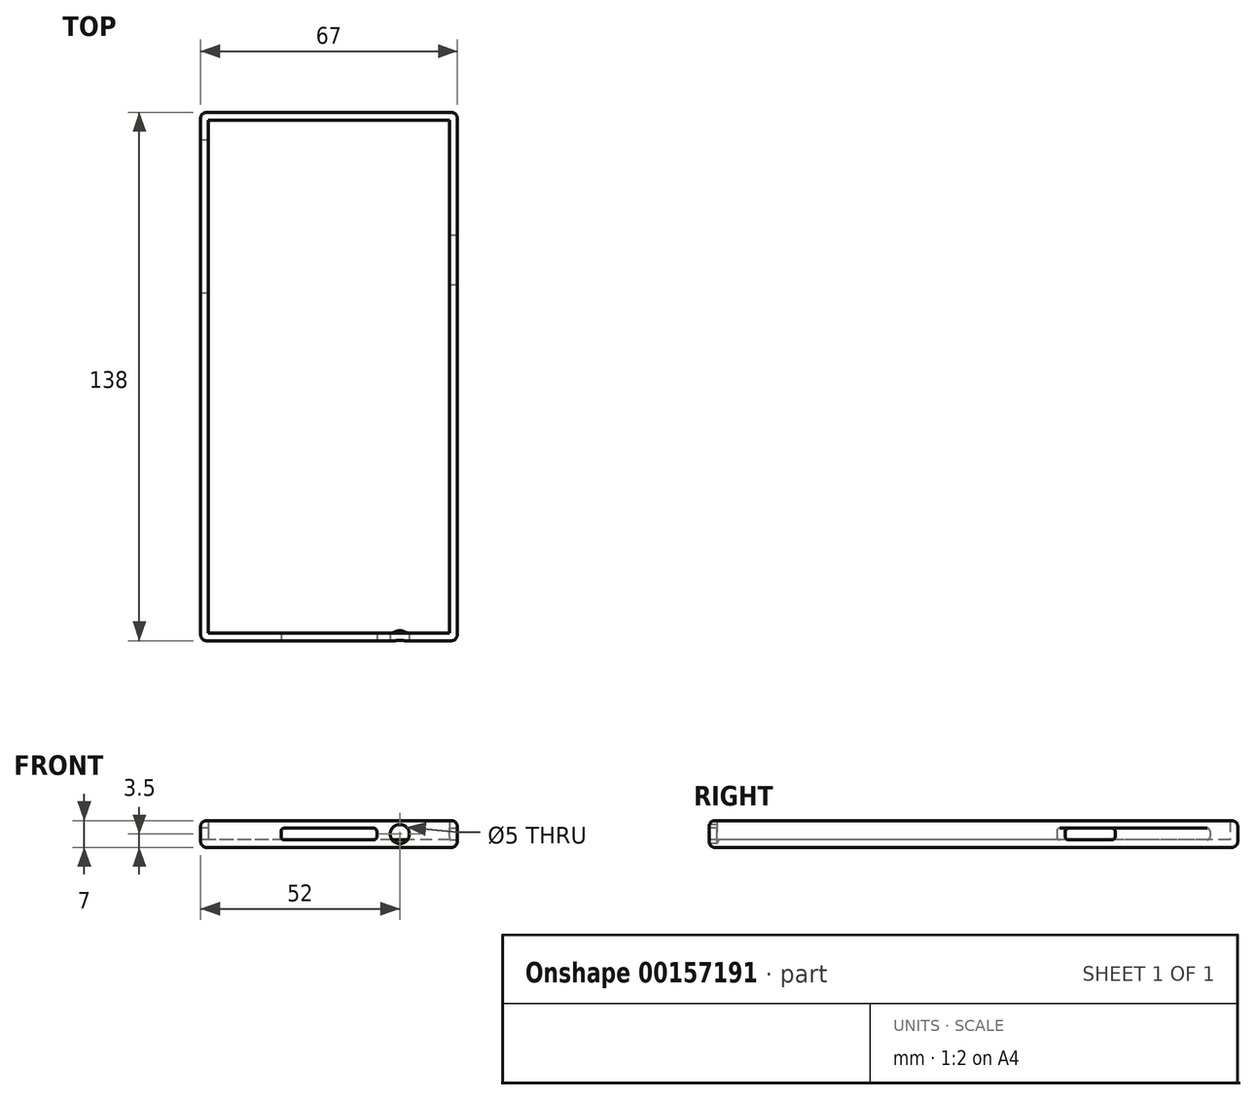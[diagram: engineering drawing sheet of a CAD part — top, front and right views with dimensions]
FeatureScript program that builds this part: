
annotation { "Feature Type Name" : "Feature", "Feature Type Description" : "" }
export const myFeature = defineFeature(function(context is Context, id is Id, definition is map)
    precondition{}
    {
        {
            var Q0;
            Q0=qCreatedBy(makeId("Top.planeOp"),FACE);
            var sketch = newSketch(context, id + "F0", { "sketchPlane" : qUnion([Q0])});
            skLineSegment(sketch, "E0.bottom", {"start": v(33.5, 69) * mm, "end": v(-33.5, 69) * mm});
            skLineSegment(sketch, "E0.top", {"start": v(33.5, -69) * mm, "end": v(-33.5, -69) * mm});
            skLineSegment(sketch, "E0.left", {"start": v(33.5, 69) * mm, "end": v(33.5, -69) * mm});
            skLineSegment(sketch, "E0.right", {"start": v(-33.5, 69) * mm, "end": v(-33.5, -69) * mm});
            skPoint(sketch, "E0.middle", {"position": v(0, 0) * mm});
            skSolve(sketch);
        }
        {
            var Q0;
            Q0 = qSketchRegion(id + "F0", true);
            extrude(context, id + "F1", {"entities" : qUnion([Q0]), "depth" : 7 * mm});
        }
        {
            var Q0;
            Q0=makeQuery(id+"F1.opExtrude","CAP_FACE",FACE,{"disambiguationData":[OSD([sQuery(id+"F0.wireOp",EDGE,"E0.bottom"),sQuery(id+"F0.wireOp",EDGE,"E0.top"),sQuery(id+"F0.wireOp",EDGE,"E0.left"),sQuery(id+"F0.wireOp",EDGE,"E0.right")])],"isStart":false});
            shell(context, id + "F2", {"entities" : qUnion([Q0]), "thickness" : 2 * mm});
        }
        {
            var Q0;
            Q0=makeQuery(id+"F1.opExtrude","SWEPT_FACE",FACE,{"disambiguationData":[OSD([sQuery(id+"F0.wireOp",EDGE,"E0.right")])]});
            var sketch = newSketch(context, id + "F3", { "sketchPlane" : qUnion([Q0])});
            skLineSegment(sketch, "E1.bottom", {"start": v(-61.02, 5) * mm, "end": v(-22.54, 5) * mm});
            skLineSegment(sketch, "E1.top", {"start": v(-61.02, 2) * mm, "end": v(-22.54, 2) * mm});
            skLineSegment(sketch, "E1.left", {"start": v(-61.78, 4.24) * mm, "end": v(-61.78, 2.76) * mm});
            skLineSegment(sketch, "E1.right", {"start": v(-21.78, 4.24) * mm, "end": v(-21.78, 2.76) * mm});
            skPoint(sketch, "E2.visualSharp", {"position": v(-61.78, 5) * mm});
            skArc(sketch, "E2.filletArc", {"start": v(-61.02, 5) * mm, "mid": v(-61.56, 4.78) * mm, "end": v(-61.78, 4.24) * mm});
            skPoint(sketch, "E3.visualSharp", {"position": v(-61.78, 2) * mm});
            skArc(sketch, "E3.filletArc", {"start": v(-61.78, 2.76) * mm, "mid": v(-61.56, 2.22) * mm, "end": v(-61.02, 2) * mm});
            skPoint(sketch, "E4.visualSharp", {"position": v(-21.78, 5) * mm});
            skArc(sketch, "E4.filletArc", {"start": v(-21.78, 4.24) * mm, "mid": v(-22, 4.78) * mm, "end": v(-22.54, 5) * mm});
            skPoint(sketch, "E5.visualSharp", {"position": v(-21.78, 2) * mm});
            skArc(sketch, "E5.filletArc", {"start": v(-22.54, 2) * mm, "mid": v(-22, 2.22) * mm, "end": v(-21.78, 2.76) * mm});
            skSolve(sketch);
        }
        {
            var Q0;
            Q0=makeQuery(id+"F3.imprint","IMPRINT",FACE,{"disambiguationData":[TD([[makeQuery(id+"F3.imprint","IMPRINT",EDGE,{"derivedFrom":sQuery(id+"F3.wireOp",EDGE,"E1.bottom")}),-1.0]])]});
            var Q1;
            Q1=makeQuery(id+"F2.opShell","OFFSET_FACE",FACE,{"disambiguationData":[OSD([sQuery(id+"F0.wireOp",EDGE,"E0.right")])]});
            extrude(context, id + "F4", {"entities" : qUnion([Q0]), "operationType" : NewBodyOperationType.REMOVE, "endBound" : BoundingType.UP_TO_SURFACE, "oppositeDirection" : true, "endBoundEntityFace" : qUnion([Q1]), "depth" : 25 * mm});
        }
        {
            var Q0;
            Q0=makeQuery(id+"F1.opExtrude","SWEPT_FACE",FACE,{"disambiguationData":[OSD([sQuery(id+"F0.wireOp",EDGE,"E0.left")])]});
            var sketch = newSketch(context, id + "F5", { "sketchPlane" : qUnion([Q0])});
            skLineSegment(sketch, "E6.bottom", {"start": v(24.76, 5) * mm, "end": v(36.24, 5) * mm});
            skLineSegment(sketch, "E6.top", {"start": v(24.76, 2) * mm, "end": v(36.24, 2) * mm});
            skLineSegment(sketch, "E6.left", {"start": v(24, 4.24) * mm, "end": v(24, 2.76) * mm});
            skLineSegment(sketch, "E6.right", {"start": v(37, 4.24) * mm, "end": v(37, 2.76) * mm});
            skPoint(sketch, "E7.visualSharp", {"position": v(24, 5) * mm});
            skArc(sketch, "E7.filletArc", {"start": v(24.76, 5) * mm, "mid": v(24.22, 4.78) * mm, "end": v(24, 4.24) * mm});
            skPoint(sketch, "E8.visualSharp", {"position": v(24, 2) * mm});
            skArc(sketch, "E8.filletArc", {"start": v(24, 2.76) * mm, "mid": v(24.22, 2.22) * mm, "end": v(24.76, 2) * mm});
            skPoint(sketch, "E9.visualSharp", {"position": v(37, 5) * mm});
            skArc(sketch, "E9.filletArc", {"start": v(37, 4.24) * mm, "mid": v(36.78, 4.78) * mm, "end": v(36.24, 5) * mm});
            skPoint(sketch, "E10.visualSharp", {"position": v(37, 2) * mm});
            skArc(sketch, "E10.filletArc", {"start": v(36.24, 2) * mm, "mid": v(36.78, 2.22) * mm, "end": v(37, 2.76) * mm});
            skSolve(sketch);
        }
        {
            var Q0;
            Q0 = qSketchRegion(id + "F5", true);
            var Q1;
            Q1=makeQuery(id+"F2.opShell","OFFSET_FACE",FACE,{"disambiguationData":[OSD([sQuery(id+"F0.wireOp",EDGE,"E0.left")])]});
            extrude(context, id + "F6", {"entities" : qUnion([Q0]), "operationType" : NewBodyOperationType.REMOVE, "endBound" : BoundingType.UP_TO_SURFACE, "oppositeDirection" : true, "endBoundEntityFace" : qUnion([Q1]), "depth" : 25 * mm});
        }
        {
            var Q0;
            Q0=makeQuery(id+"F1.opExtrude","SWEPT_FACE",FACE,{"disambiguationData":[OSD([sQuery(id+"F0.wireOp",EDGE,"E0.top")])]});
            var sketch = newSketch(context, id + "F7", { "sketchPlane" : qUnion([Q0])});
            skLineSegment(sketch, "E11.bottom", {"start": v(-11.74, 5) * mm, "end": v(11.74, 5) * mm});
            skLineSegment(sketch, "E11.top", {"start": v(-11.74, 2) * mm, "end": v(11.74, 2) * mm});
            skLineSegment(sketch, "E11.left", {"start": v(-12.5, 4.24) * mm, "end": v(-12.5, 2.76) * mm});
            skLineSegment(sketch, "E11.right", {"start": v(12.5, 4.24) * mm, "end": v(12.5, 2.76) * mm});
            skPoint(sketch, "E12", {"position": v(0, 5) * mm});
            skPoint(sketch, "E13", {"position": v(0, 7) * mm});
            skPoint(sketch, "E14.visualSharp", {"position": v(-12.5, 5) * mm});
            skArc(sketch, "E14.filletArc", {"start": v(-11.74, 5) * mm, "mid": v(-12.28, 4.78) * mm, "end": v(-12.5, 4.24) * mm});
            skPoint(sketch, "E15.visualSharp", {"position": v(-12.5, 2) * mm});
            skArc(sketch, "E15.filletArc", {"start": v(-12.5, 2.76) * mm, "mid": v(-12.28, 2.22) * mm, "end": v(-11.74, 2) * mm});
            skPoint(sketch, "E16.visualSharp", {"position": v(12.5, 5) * mm});
            skArc(sketch, "E16.filletArc", {"start": v(12.5, 4.24) * mm, "mid": v(12.28, 4.78) * mm, "end": v(11.74, 5) * mm});
            skPoint(sketch, "E17.visualSharp", {"position": v(12.5, 2) * mm});
            skArc(sketch, "E17.filletArc", {"start": v(11.74, 2) * mm, "mid": v(12.28, 2.22) * mm, "end": v(12.5, 2.76) * mm});
            skSolve(sketch);
        }
        {
            var Q0;
            Q0 = qSketchRegion(id + "F7", true);
            var Q1;
            Q1=makeQuery(id+"F2.opShell","OFFSET_FACE",FACE,{"disambiguationData":[OSD([sQuery(id+"F0.wireOp",EDGE,"E0.top")])]});
            extrude(context, id + "F8", {"entities" : qUnion([Q0]), "operationType" : NewBodyOperationType.REMOVE, "endBound" : BoundingType.UP_TO_SURFACE, "oppositeDirection" : true, "endBoundEntityFace" : qUnion([Q1]), "depth" : 25 * mm});
        }
        {
            var Q0;
            Q0=makeQuery(id+"F1.opExtrude","SWEPT_FACE",FACE,{"disambiguationData":[OSD([sQuery(id+"F0.wireOp",EDGE,"E0.top")])]});
            var sketch = newSketch(context, id + "F9", { "sketchPlane" : qUnion([Q0])});
            skPoint(sketch, "E18", {"position": v(18.5, 3.5) * mm});
            skPoint(sketch, "E18.positionSnap0", {"position": v(33.5, 3.5) * mm});
            skSolve(sketch);
        }
        {
            var Q0;
            Q0=sQuery(id+"F9.wireOp",VERTEX,"E18");
            var Q1;
            Q1=makeQuery(id+"F1.opExtrude","SWEPT_BODY",BODY,{"disambiguationData":[OSD([sQuery(id+"F0.wireOp",EDGE,"E0.bottom"),sQuery(id+"F0.wireOp",EDGE,"E0.top"),sQuery(id+"F0.wireOp",EDGE,"E0.left"),sQuery(id+"F0.wireOp",EDGE,"E0.right")])]});
            hole(context, id + "F10", {"style" : HoleStyle.SIMPLE, "endStyle" : HoleEndStyle.BLIND, "holeDiameter" : 5 * mm, "holeDepth" : 2 * mm, "locations" : qUnion([Q0]), "scope" : qUnion([Q1])});
        }
        {
            var Q0;
            Q0=makeQuery(id+"F1.opExtrude","CAP_EDGE",EDGE,{"disambiguationData":[OSD([sQuery(id+"F0.wireOp",EDGE,"E0.left")])],"isStart":false});
            var Q1;
            Q1=makeQuery(id+"F1.opExtrude","CAP_EDGE",EDGE,{"disambiguationData":[OSD([sQuery(id+"F0.wireOp",EDGE,"E0.top")])],"isStart":false});
            var Q2;
            Q2=makeQuery(id+"F1.opExtrude","CAP_EDGE",EDGE,{"disambiguationData":[OSD([sQuery(id+"F0.wireOp",EDGE,"E0.top")])],"isStart":true});
            var Q3;
            Q3=makeQuery(id+"F1.opExtrude","SWEPT_EDGE",EDGE,{"disambiguationData":[OSD([sQuery(id+"F0.wireOp",EDGE,"E0.top"),sQuery(id+"F0.wireOp",EDGE,"E0.left")])]});
            var Q4;
            Q4=makeQuery(id+"F1.opExtrude","CAP_EDGE",EDGE,{"disambiguationData":[OSD([sQuery(id+"F0.wireOp",EDGE,"E0.left")])],"isStart":true});
            var Q5;
            Q5=makeQuery(id+"F1.opExtrude","SWEPT_EDGE",EDGE,{"disambiguationData":[OSD([sQuery(id+"F0.wireOp",EDGE,"E0.bottom"),sQuery(id+"F0.wireOp",EDGE,"E0.left")])]});
            var Q6;
            Q6=makeQuery(id+"F1.opExtrude","CAP_EDGE",EDGE,{"disambiguationData":[OSD([sQuery(id+"F0.wireOp",EDGE,"E0.bottom")])],"isStart":false});
            var Q7;
            Q7=makeQuery(id+"F1.opExtrude","CAP_EDGE",EDGE,{"disambiguationData":[OSD([sQuery(id+"F0.wireOp",EDGE,"E0.bottom")])],"isStart":true});
            var Q8;
            Q8=makeQuery(id+"F1.opExtrude","SWEPT_EDGE",EDGE,{"disambiguationData":[OSD([sQuery(id+"F0.wireOp",EDGE,"E0.bottom"),sQuery(id+"F0.wireOp",EDGE,"E0.right")])]});
            var Q9;
            Q9=makeQuery(id+"F1.opExtrude","CAP_EDGE",EDGE,{"disambiguationData":[OSD([sQuery(id+"F0.wireOp",EDGE,"E0.right")])],"isStart":false});
            var Q10;
            Q10=makeQuery(id+"F1.opExtrude","CAP_EDGE",EDGE,{"disambiguationData":[OSD([sQuery(id+"F0.wireOp",EDGE,"E0.right")])],"isStart":true});
            var Q11;
            Q11=makeQuery(id+"F1.opExtrude","SWEPT_EDGE",EDGE,{"disambiguationData":[OSD([sQuery(id+"F0.wireOp",EDGE,"E0.top"),sQuery(id+"F0.wireOp",EDGE,"E0.right")])]});
            fillet(context, id + "F11", {"entities" : qUnion([Q0, Q1, Q2, Q3, Q4, Q5, Q6, Q7, Q8, Q9, Q10, Q11]), "radius" : 1.5 * mm, "tangentPropagation" : true, "allowEdgeOverflow" : false});
        }
    });
